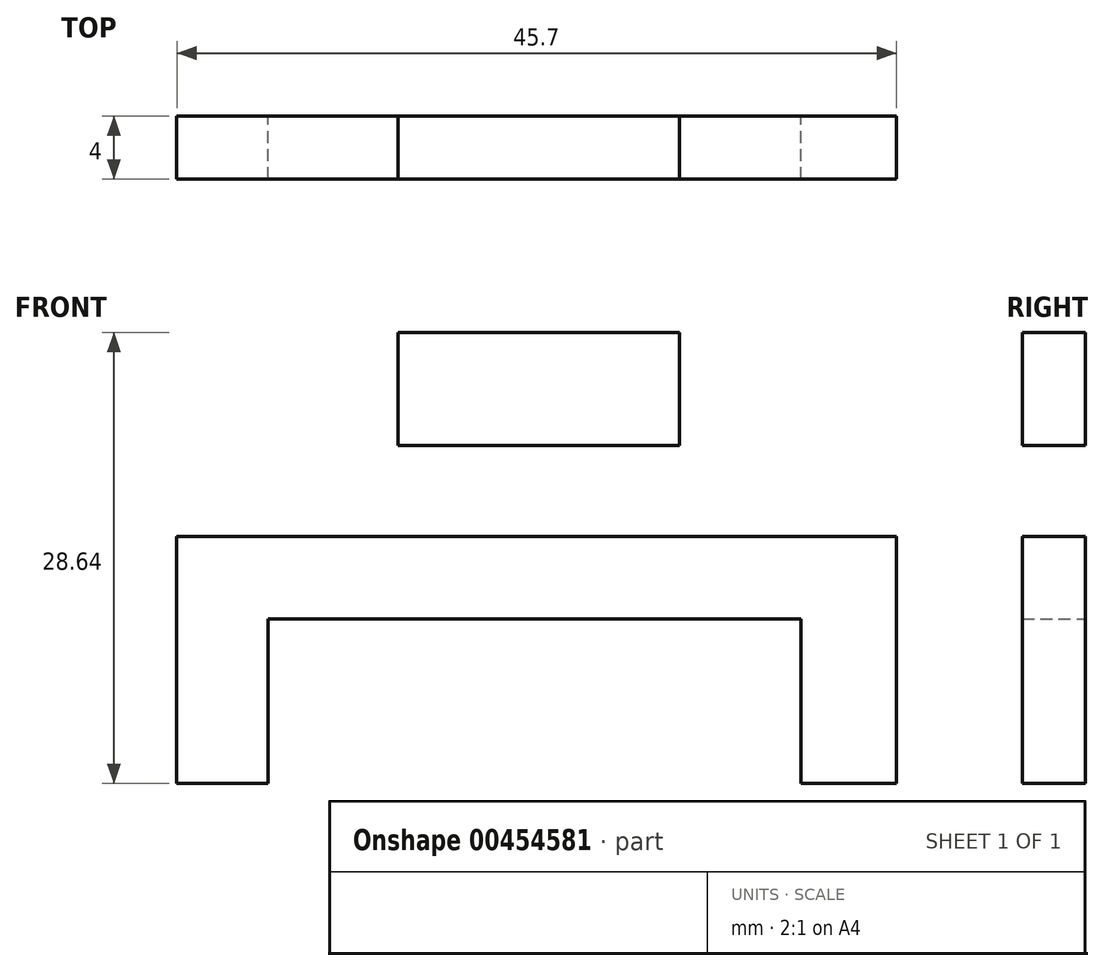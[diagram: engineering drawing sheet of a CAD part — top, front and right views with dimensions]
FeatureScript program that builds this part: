
annotation { "Feature Type Name" : "Feature", "Feature Type Description" : "" }
export const myFeature = defineFeature(function(context is Context, id is Id, definition is map)
    precondition{}
    {
        {
            var Q0;
            Q0=qCreatedBy(makeId("Front.planeOp"),FACE);
            var sketch = newSketch(context, id + "F0", { "sketchPlane" : qUnion([Q0])});
            skLineSegment(sketch, "E0.bottom", {"start": v(-17.07, 0) * mm, "end": v(16.8, 0) * mm});
            skLineSegment(sketch, "E0.top", {"start": v(-17.07, 10.46) * mm, "end": v(16.8, 10.46) * mm});
            skLineSegment(sketch, "E0.left", {"start": v(-17.07, 0) * mm, "end": v(-17.07, 10.46) * mm});
            skLineSegment(sketch, "E0.right", {"start": v(16.8, 0) * mm, "end": v(16.8, 10.46) * mm});
            skLineSegment(sketch, "E1.bottom", {"start": v(-22.85, 0) * mm, "end": v(22.85, 0) * mm});
            skLineSegment(sketch, "E1.top", {"start": v(-22.85, 15.7) * mm, "end": v(22.85, 15.7) * mm});
            skLineSegment(sketch, "E1.left", {"start": v(-22.85, 0) * mm, "end": v(-22.85, 15.7) * mm});
            skLineSegment(sketch, "E1.right", {"start": v(22.85, 0) * mm, "end": v(22.85, 15.7) * mm});
            skLineSegment(sketch, "E2.bottom", {"start": v(-8.81, 28.64) * mm, "end": v(9.09, 28.64) * mm});
            skLineSegment(sketch, "E2.top", {"start": v(-8.81, 21.48) * mm, "end": v(9.09, 21.48) * mm});
            skLineSegment(sketch, "E2.left", {"start": v(-8.81, 28.64) * mm, "end": v(-8.81, 21.48) * mm});
            skLineSegment(sketch, "E2.right", {"start": v(9.09, 28.64) * mm, "end": v(9.09, 21.48) * mm});
            skLineSegment(sketch, "E3.bottom", {"start": v(-3.58, 21.48) * mm, "end": v(3.85, 21.48) * mm});
            skLineSegment(sketch, "E3.top", {"start": v(-3.58, 15.7) * mm, "end": v(3.85, 15.7) * mm});
            skLineSegment(sketch, "E3.left", {"start": v(-3.58, 21.48) * mm, "end": v(-3.58, 15.7) * mm});
            skLineSegment(sketch, "E3.right", {"start": v(3.85, 21.48) * mm, "end": v(3.85, 15.7) * mm});
            skSolve(sketch);
        }
        {
            var Q0;
            Q0=makeQuery(id+"F0.imprint","IMPRINT",FACE,{"disambiguationData":[TD([[makeQuery(id+"F0.imprint","IMPRINT",EDGE,{"derivedFrom":sQuery(id+"F0.wireOp",EDGE,"E0.top")}),1.0]])]});
            var Q1;
            Q1=makeQuery(id+"F0.imprint","IMPRINT",FACE,{"disambiguationData":[TD([[makeQuery(id+"F0.imprint","IMPRINT",EDGE,{"derivedFrom":sQuery(id+"F0.wireOp",EDGE,"E3.bottom")}),-1.0]])]});
            var Q2;
            Q2=makeQuery(id+"F0.imprint","IMPRINT",FACE,{"disambiguationData":[TD([[makeQuery(id+"F0.imprint","IMPRINT",EDGE,{"derivedFrom":sQuery(id+"F0.wireOp",EDGE,"E2.bottom")}),-1.0]])]});
            extrude(context, id + "F1", {"entities" : qUnion([Q0, Q1, Q2]), "depth" : 4 * mm});
        }
    });
